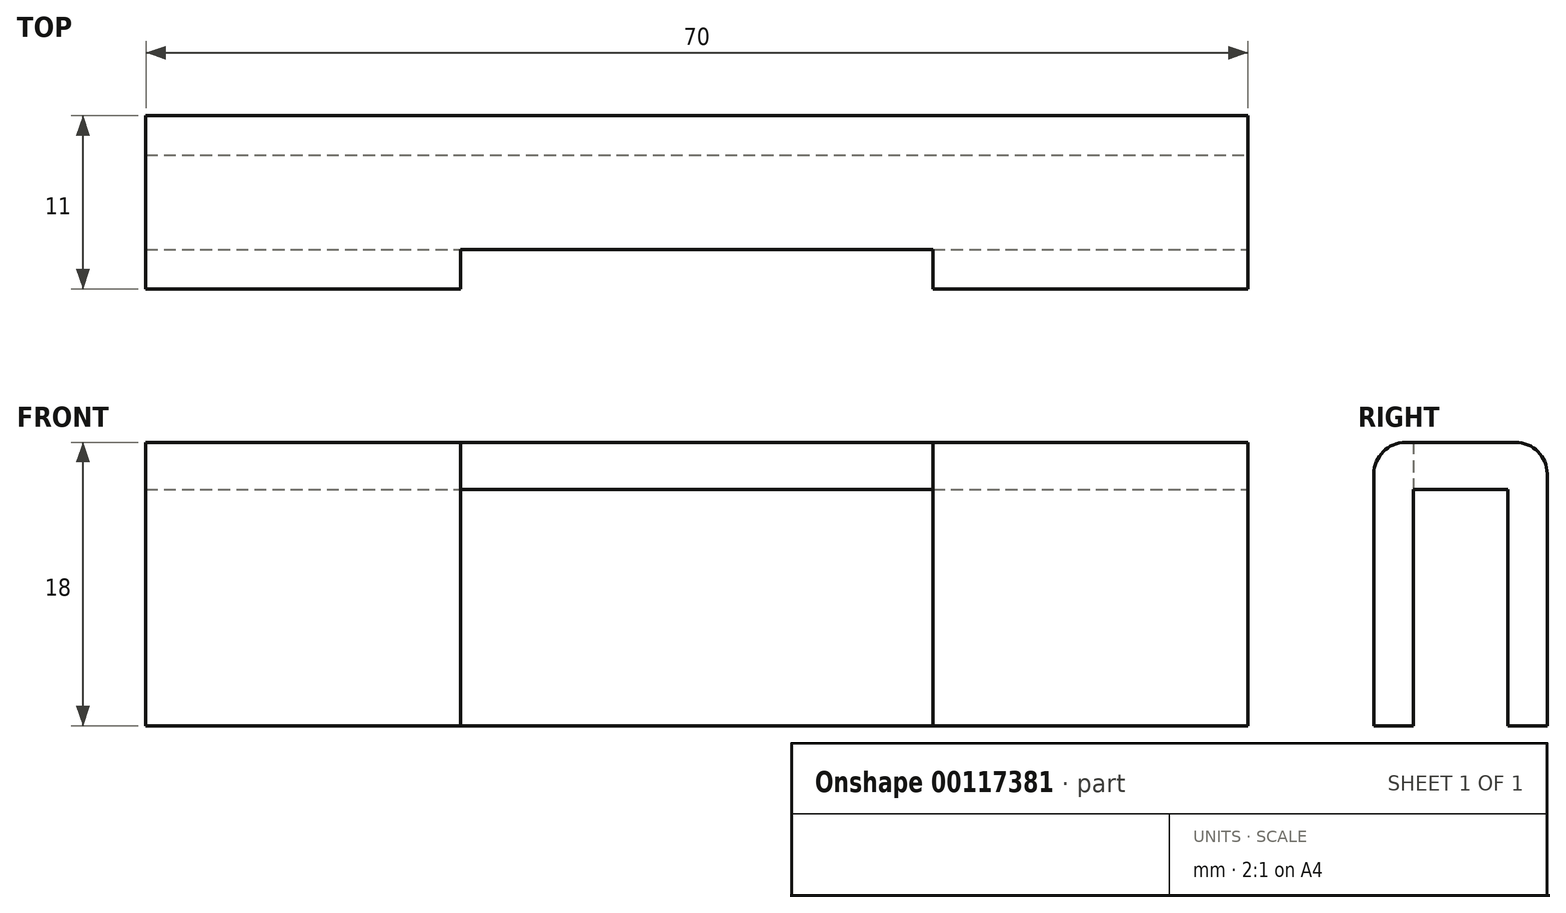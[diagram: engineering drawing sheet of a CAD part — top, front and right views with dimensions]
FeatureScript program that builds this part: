
annotation { "Feature Type Name" : "Feature", "Feature Type Description" : "" }
export const myFeature = defineFeature(function(context is Context, id is Id, definition is map)
    precondition{}
    {
        {
            var Q0;
            Q0=qCreatedBy(makeId("Top.planeOp"),FACE);
            var sketch = newSketch(context, id + "F0", { "sketchPlane" : qUnion([Q0])});
            skLineSegment(sketch, "E0.bottom", {"start": v(-24.26, -22.1) * mm, "end": v(45.74, -22.1) * mm});
            skLineSegment(sketch, "E0.top", {"start": v(-24.26, -16.1) * mm, "end": v(45.74, -16.1) * mm});
            skLineSegment(sketch, "E0.left", {"start": v(-24.26, -22.1) * mm, "end": v(-24.26, -16.1) * mm});
            skLineSegment(sketch, "E0.right", {"start": v(45.74, -22.1) * mm, "end": v(45.74, -16.1) * mm});
            skLineSegment(sketch, "E1", {"start": v(-24.26, -16.1) * mm, "end": v(-24.26, -13.6) * mm});
            skLineSegment(sketch, "E2", {"start": v(-24.26, -13.6) * mm, "end": v(45.74, -13.6) * mm});
            skLineSegment(sketch, "E3", {"start": v(45.74, -16.1) * mm, "end": v(45.74, -13.6) * mm});
            skLineSegment(sketch, "E4", {"start": v(-24.26, -22.1) * mm, "end": v(-24.26, -24.6) * mm});
            skLineSegment(sketch, "E5", {"start": v(-24.26, -24.6) * mm, "end": v(-4.26, -24.6) * mm});
            skLineSegment(sketch, "E6", {"start": v(-4.26, -24.6) * mm, "end": v(-4.26, -22.1) * mm});
            skLineSegment(sketch, "E7", {"start": v(45.74, -22.1) * mm, "end": v(45.74, -24.6) * mm});
            skLineSegment(sketch, "E8", {"start": v(45.74, -24.6) * mm, "end": v(25.74, -24.6) * mm});
            skLineSegment(sketch, "E9", {"start": v(25.74, -24.6) * mm, "end": v(25.74, -22.1) * mm});
            skSolve(sketch);
        }
        {
            var Q0;
            Q0=makeQuery(id+"F0.imprint","IMPRINT",FACE,{"disambiguationData":[TD([[makeQuery(id+"F0.imprint","IMPRINT",EDGE,{"derivedFrom":sQuery(id+"F0.wireOp",EDGE,"E0.bottom")}),1.0]])]});
            extrude(context, id + "F1", {"entities" : qUnion([Q0]), "depth" : 3 * mm});
        }
        {
            var Q0;
            {var subQ0=sQuery(id+"F0.wireOp",EDGE,"E4");Q0=makeQuery(id+"F0.imprint","IMPRINT",FACE,{"disambiguationData":[TD([[makeQuery(id+"F0.imprint","IMPRINT",EDGE,{"derivedFrom":subQ0}),1.0]])]});}
            var Q1;
            {var subQ0=sQuery(id+"F0.wireOp",EDGE,"E7");Q1=makeQuery(id+"F0.imprint","IMPRINT",FACE,{"disambiguationData":[TD([[makeQuery(id+"F0.imprint","IMPRINT",EDGE,{"derivedFrom":subQ0}),-1.0]])]});}
            var Q2;
            Q2=makeQuery(id+"F0.imprint","IMPRINT",FACE,{"disambiguationData":[TD([[makeQuery(id+"F0.imprint","IMPRINT",EDGE,{"derivedFrom":sQuery(id+"F0.wireOp",EDGE,"E0.top")}),1.0]])]});
            extrude(context, id + "F2", {"entities" : qUnion([Q0, Q1, Q2]), "operationType" : NewBodyOperationType.ADD, "depth" : 3 * mm});
        }
        {
            var Q0;
            Q0=makeQuery(id+"F0.imprint","IMPRINT",FACE,{"disambiguationData":[TD([[makeQuery(id+"F0.imprint","IMPRINT",EDGE,{"derivedFrom":sQuery(id+"F0.wireOp",EDGE,"E0.top")}),1.0]])]});
            var Q1;
            {var subQ0=sQuery(id+"F0.wireOp",EDGE,"E4");Q1=makeQuery(id+"F0.imprint","IMPRINT",FACE,{"disambiguationData":[TD([[makeQuery(id+"F0.imprint","IMPRINT",EDGE,{"derivedFrom":subQ0}),1.0]])]});}
            var Q2;
            {var subQ0=sQuery(id+"F0.wireOp",EDGE,"E7");Q2=makeQuery(id+"F0.imprint","IMPRINT",FACE,{"disambiguationData":[TD([[makeQuery(id+"F0.imprint","IMPRINT",EDGE,{"derivedFrom":subQ0}),-1.0]])]});}
            extrude(context, id + "F3", {"entities" : qUnion([Q0, Q1, Q2]), "operationType" : NewBodyOperationType.ADD, "oppositeDirection" : true, "depth" : 15 * mm});
        }
        {
            var Q0;
            Q0=makeQuery(id+"F2.opExtrude","CAP_EDGE",EDGE,{"disambiguationData":[OSD([sQuery(id+"F0.wireOp",EDGE,"E2")])],"isStart":false});
            var Q1;
            Q1=makeQuery(id+"F2.opExtrude","CAP_EDGE",EDGE,{"disambiguationData":[OSD([sQuery(id+"F0.wireOp",EDGE,"E5")])],"isStart":false});
            var Q2;
            Q2=makeQuery(id+"F2.opExtrude","CAP_EDGE",EDGE,{"disambiguationData":[OSD([sQuery(id+"F0.wireOp",EDGE,"E8")])],"isStart":false});
            fillet(context, id + "F4", {"entities" : qUnion([Q0, Q1, Q2]), "radius" : 2 * mm, "tangentPropagation" : true, "allowEdgeOverflow" : false});
        }
    });
